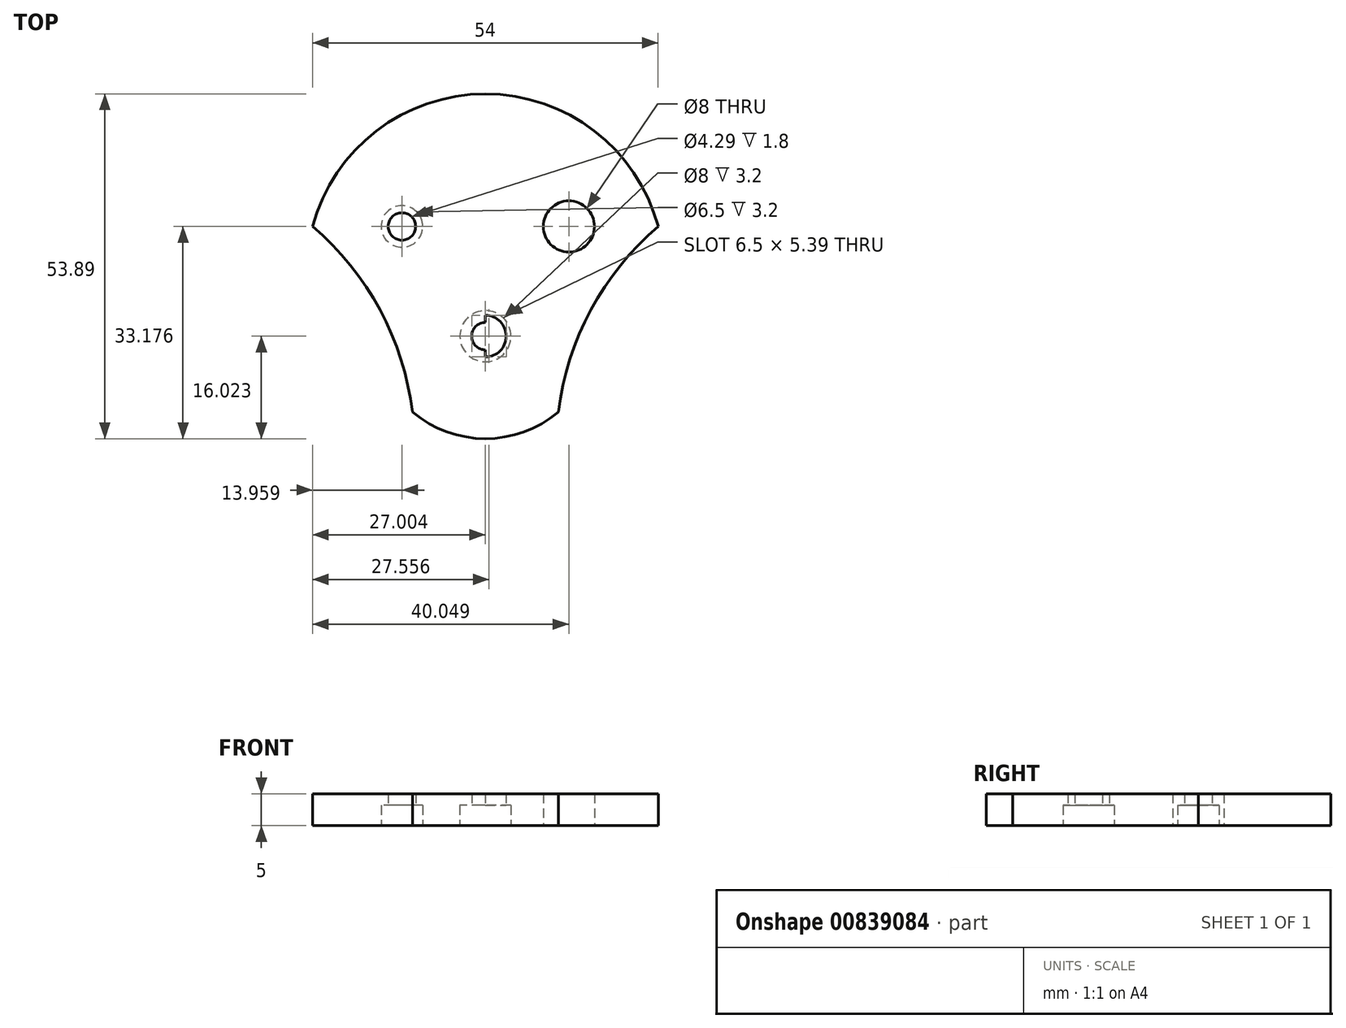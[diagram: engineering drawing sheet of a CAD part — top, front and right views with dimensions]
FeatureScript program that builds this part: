
annotation { "Feature Type Name" : "Feature", "Feature Type Description" : "" }
export const myFeature = defineFeature(function(context is Context, id is Id, definition is map)
    precondition{}
    {
        {
            var Q0;
            Q0=qCreatedBy(makeId("Top.planeOp"),FACE);
            var sketch = newSketch(context, id + "F0", { "sketchPlane" : qUnion([Q0])});
            skLineSegment(sketch, "E0", {"start": v(0.75, -57.31) * mm, "end": v(0.75, -43.31) * mm});
            skCircle(sketch, "E1", {"center": v(0.75, -41.17) * mm, "radius": 2.15 * mm});
            skLineSegment(sketch, "E2", {"start": v(0.75, -39.02) * mm, "end": v(0.75, -24.01) * mm});
            skLineSegment(sketch, "E3", {"start": v(0.75, -24.01) * mm, "end": v(-10.15, -24.01) * mm});
            skLineSegment(sketch, "E4", {"start": v(0.75, -24.01) * mm, "end": v(11.65, -24.01) * mm});
            skCircle(sketch, "E5", {"center": v(-12.3, -24.01) * mm, "radius": 2.15 * mm});
            skCircle(sketch, "E6", {"center": v(13.8, -24.01) * mm, "radius": 2.15 * mm});
            skCircle(sketch, "E7", {"center": v(-12.3, -24.01) * mm, "radius": 3.25 * mm});
            skCircle(sketch, "E8", {"center": v(13.8, -24.01) * mm, "radius": 3.25 * mm});
            skCircle(sketch, "E9", {"center": v(0.75, -41.17) * mm, "radius": 3.25 * mm});
            skArc(sketch, "E10", {"start": v(27.75, -24.01) * mm, "mid": v(0.75, -3.3) * mm, "end": v(-26.25, -24.01) * mm});
            skArc(sketch, "E11", {"start": v(-10.66, -53.02) * mm, "mid": v(-15.72, -37.05) * mm, "end": v(-26.25, -24.01) * mm});
            skArc(sketch, "E12.MirrorCS", {"start": v(-26.25, -24.01) * mm, "mid": v(0.75, -3.3) * mm, "end": v(27.75, -24.01) * mm});
            skArc(sketch, "E13.MirrorCS", {"start": v(12.17, -53.02) * mm, "mid": v(17.23, -37.05) * mm, "end": v(27.75, -24.01) * mm});
            skArc(sketch, "E14", {"start": v(-10.66, -53.02) * mm, "mid": v(0.75, -57.19) * mm, "end": v(12.17, -53.02) * mm});
            skCircle(sketch, "E15", {"center": v(-12.3, -24.01) * mm, "radius": 4 * mm});
            skCircle(sketch, "E16", {"center": v(13.8, -24.01) * mm, "radius": 4 * mm});
            skCircle(sketch, "E17", {"center": v(0.75, -41.17) * mm, "radius": 4 * mm});
            skSolve(sketch);
        }
        {
            var Q0;
            Q0 = qSketchRegion(id + "F0", true);
            var Q1;
            Q1=makeQuery(id+"F0.imprint","IMPRINT",FACE,{"disambiguationData":[TD([[makeQuery(id+"F0.imprint","IMPRINT",EDGE,{"derivedFrom":sQuery(id+"F0.wireOp",EDGE,"E6")}),1.0]])]});
            var Q2;
            Q2=makeQuery(id+"F0.imprint","IMPRINT",FACE,{"disambiguationData":[TD([[makeQuery(id+"F0.imprint","IMPRINT",EDGE,{"derivedFrom":sQuery(id+"F0.wireOp",EDGE,"E5")}),-1.0]])]});
            var Q3;
            {var subQ0=sQuery(id+"F0.wireOp",EDGE,"E1");var subQ1=sQuery(id+"F0.wireOp",EDGE,"E2");var subQ2=makeQuery(id+"F0.imprint","INTERSECT",VERTEX,{"derivedFrom":[subQ1,subQ0]});Q3=makeQuery(id+"F0.imprint","IMPRINT",FACE,{"disambiguationData":[TD([[makeQuery(id+"F0.imprint","IMPRINT",EDGE,{"disambiguationData":[TD([[subQ2,-1.0]])],"derivedFrom":subQ1}),1.0]])]});}
            var Q4;
            Q4=makeQuery(id+"F0.imprint","IMPRINT",FACE,{"disambiguationData":[TD([[makeQuery(id+"F0.imprint","IMPRINT",EDGE,{"derivedFrom":sQuery(id+"F0.wireOp",EDGE,"E8")}),1.0]])]});
            var Q5;
            {var subQ0=sQuery(id+"F0.wireOp",EDGE,"E17");var subQ1=sQuery(id+"F0.wireOp",EDGE,"E2");var subQ2=makeQuery(id+"F0.imprint","INTERSECT",VERTEX,{"derivedFrom":[subQ1,subQ0]});Q5=makeQuery(id+"F0.imprint","IMPRINT",FACE,{"disambiguationData":[TD([[makeQuery(id+"F0.imprint","IMPRINT",EDGE,{"disambiguationData":[TD([[subQ2,1.0]])],"derivedFrom":subQ1}),1.0]])]});}
            var Q6;
            {var subQ0=sQuery(id+"F0.wireOp",EDGE,"E1");var subQ1=sQuery(id+"F0.wireOp",EDGE,"E2");var subQ2=makeQuery(id+"F0.imprint","INTERSECT",VERTEX,{"derivedFrom":[subQ1,subQ0]});Q6=makeQuery(id+"F0.imprint","IMPRINT",FACE,{"disambiguationData":[TD([[makeQuery(id+"F0.imprint","IMPRINT",EDGE,{"disambiguationData":[TD([[subQ2,-1.0]])],"derivedFrom":subQ1}),-1.0]])]});}
            var Q7;
            {var subQ0=sQuery(id+"F0.wireOp",EDGE,"E17");var subQ1=sQuery(id+"F0.wireOp",EDGE,"E2");var subQ2=makeQuery(id+"F0.imprint","INTERSECT",VERTEX,{"derivedFrom":[subQ1,subQ0]});Q7=makeQuery(id+"F0.imprint","IMPRINT",FACE,{"disambiguationData":[TD([[makeQuery(id+"F0.imprint","IMPRINT",EDGE,{"disambiguationData":[TD([[subQ2,1.0]])],"derivedFrom":subQ1}),-1.0]])]});}
            var Q8;
            Q8=makeQuery(id+"F0.imprint","IMPRINT",FACE,{"disambiguationData":[TD([[makeQuery(id+"F0.imprint","IMPRINT",EDGE,{"derivedFrom":sQuery(id+"F0.wireOp",EDGE,"E7")}),-1.0]])]});
            extrude(context, id + "F1", {"entities" : qUnion([Q0, Q1, Q2, Q3, Q4, Q5, Q6, Q7, Q8]), "depth" : 5 * mm, "offsetDistance" : 25 * mm});
        }
        {
            var Q0;
            Q0=makeQuery(id+"F0.imprint","IMPRINT",FACE,{"disambiguationData":[TD([[makeQuery(id+"F0.imprint","IMPRINT",EDGE,{"derivedFrom":sQuery(id+"F0.wireOp",EDGE,"E6")}),1.0]])]});
            var Q1;
            Q1=makeQuery(id+"F0.imprint","IMPRINT",FACE,{"disambiguationData":[TD([[makeQuery(id+"F0.imprint","IMPRINT",EDGE,{"derivedFrom":sQuery(id+"F0.wireOp",EDGE,"E5")}),-1.0]])]});
            var Q2;
            {var subQ0=sQuery(id+"F0.wireOp",EDGE,"E1");var subQ1=sQuery(id+"F0.wireOp",EDGE,"E2");var subQ2=makeQuery(id+"F0.imprint","INTERSECT",VERTEX,{"derivedFrom":[subQ1,subQ0]});Q2=makeQuery(id+"F0.imprint","IMPRINT",FACE,{"disambiguationData":[TD([[makeQuery(id+"F0.imprint","IMPRINT",EDGE,{"disambiguationData":[TD([[subQ2,-1.0]])],"derivedFrom":subQ1}),1.0]])]});}
            var Q3;
            {var subQ0=sQuery(id+"F0.wireOp",EDGE,"E1");var subQ1=sQuery(id+"F0.wireOp",EDGE,"E2");var subQ2=makeQuery(id+"F0.imprint","INTERSECT",VERTEX,{"derivedFrom":[subQ1,subQ0]});Q3=makeQuery(id+"F0.imprint","IMPRINT",FACE,{"disambiguationData":[TD([[makeQuery(id+"F0.imprint","IMPRINT",EDGE,{"disambiguationData":[TD([[subQ2,-1.0]])],"derivedFrom":subQ1}),-1.0]])]});}
            var Q4;
            Q4=sQuery(id+"F0.wireOp",EDGE,"E8");
            var Q5;
            Q5=sQuery(id+"F0.wireOp",EDGE,"E7");
            var Q6;
            Q6=sQuery(id+"F0.wireOp",EDGE,"E9");
            extrude(context, id + "F2", {"entities" : qUnion([Q0, Q1, Q2, Q3]), "operationType" : NewBodyOperationType.REMOVE, "surfaceEntities" : qUnion([Q4, Q5, Q6]), "depth" : 3.2 * mm, "offsetDistance" : 25 * mm});
        }
    });
